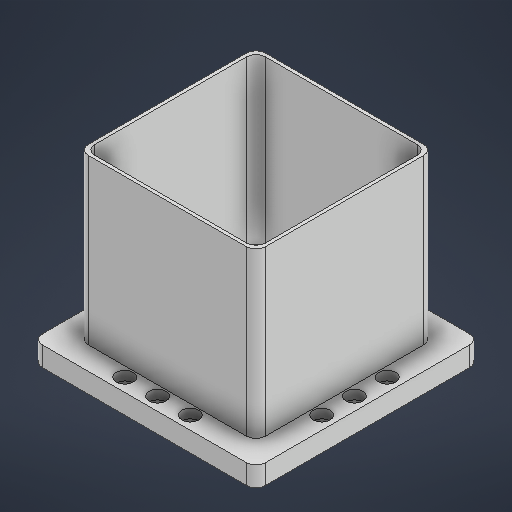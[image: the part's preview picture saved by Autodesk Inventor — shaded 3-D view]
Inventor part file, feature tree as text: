
AUTODESK INVENTOR PART (.ipt)
format: ipt  version: 2025 (Build 290162000, 162)  size: 280,064 bytes
history: native  units: in
note: dims shown in document units (in); Inventor stores cm internally (conversion verified against a paired STEP export)
features: sketch x3, extrude x2, hole x1, fillet x1
ambient origin geometry x8: Origin, YZ Plane, XZ Plane, XY Plane, X Axis, Y Axis, Z Axis, Center Point
bodies: Solid1 (feature_tree)
feature tree (7):
  extrude  "Extrusion1"  Depth=5.9055in
  hole  "Hole1"  [1 undecoded]
  extrude  "Extrusion3"  Depth=0.2805in
  fillet  "Fillet2"  Radius=0.2362in
  sketch  "Sketch1"  dims[d17=0.5906in d18=0.0in d30=5.9055in]
  sketch  "Sketch3"  dims[d31=5.9055in d32=0.2362in]
  sketch  "Sketch4"  dims[d33=0.2362in d34=0.2362in d35=0.2362in d36=0.2362in d37=0.2362in d38=0.9843in d39=0.9843in d40=0.9843in d41=0.9843in d42=0.2805in d43=0.2362in d44=0.5118in d45=0.2756in d46=0.0172in d47=0.315in d48=0.8108in d50=1.7717in d51=6.6929in d52=6.6929in d53=0.7874in d54=5.1181in d55=5.1181in d56=1.7717in d57=5.1181in d58=5.1181in d59=0.0984in d60=4.9213in d61=0.0in d62=0.0787in d63=0.7874in d64=0.7087in d65=0.2805in d66=0.0in d67=0.0in d68=0.0in d69=0.0in]
note: 1 required parameter value undecoded (feature->parameter linkage not recoverable at this tier; creation-order binding heuristic only, values carry confidence <= 0.55)
